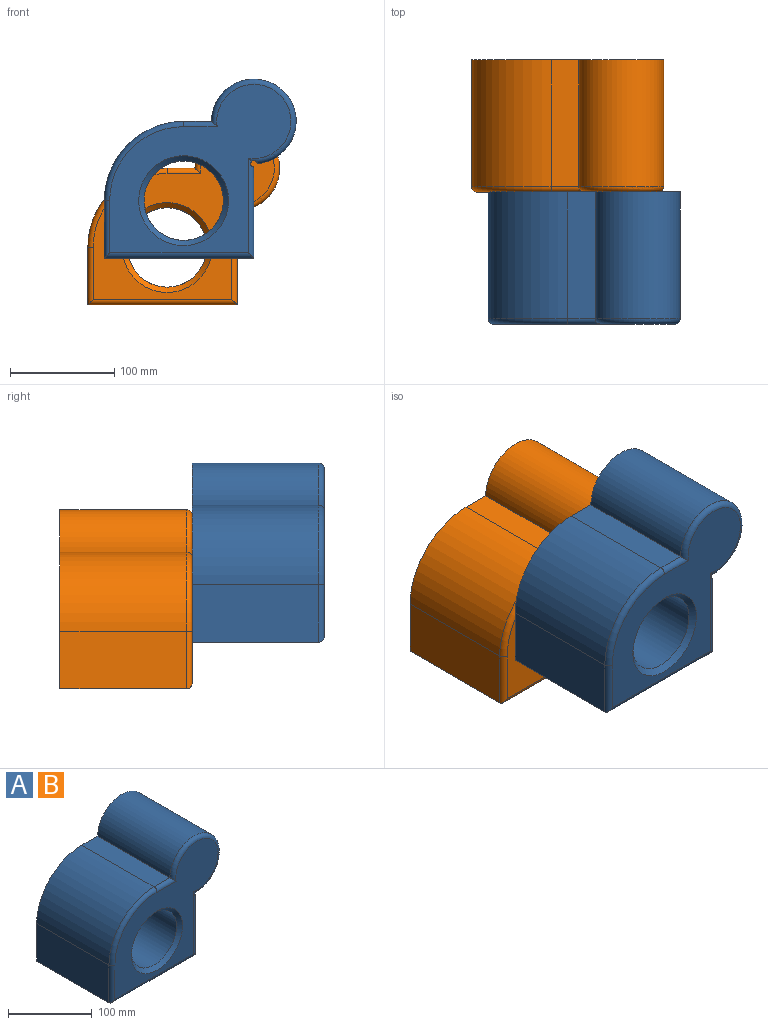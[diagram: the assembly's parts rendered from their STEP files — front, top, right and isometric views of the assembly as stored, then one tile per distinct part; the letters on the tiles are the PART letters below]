
ASSEMBLY  parts=2 mates=1
PART A: 17 faces, bbox 194x127x175.5 mm
  f0: plane 121.92x87.55mm, normal (1,0,0), area 10673.5mm2, adj f3,f7,f9,f14
  f1: cylinder r=40.72mm len=121.92mm, axis (0,1,0), area 23007.2mm2, adj f2,f4,f9,f14
  f2: torus R=35.64mm, axis (0,-1,0), area 1469.4mm2, adj f1,f3,f8,f10,f14
  f3: cylinder r=5.08mm len=96.16mm, axis (0,0,-1), area 702.5mm2, adj f0,f2,f8,f12,f14
  f4: plane 121.92x26.72mm, normal (0,0,1), area 3258mm2, adj f1,f5,f9,f10
  f5: cylinder r=76.2mm len=121.92mm, axis (0,1,0), area 14593.2mm2, adj f4,f6,f9,f11
  f6: plane 121.92x55.24mm, normal (-1,0,0), area 6734.7mm2, adj f5,f7,f9,f13
  f7: plane 143.64x121.92mm, normal (0,0,-1), area 17512.7mm2, adj f0,f6,f9,f12
  f8: plane 174.2x162mm, normal (0,-1,0), area 12573.2mm2, adj f2,f3,f10,f11,f12,f13,f16
  f9: plane 184.36x172.16mm, normal (0,1,0), area 16956.6mm2, adj f0,f1,f4,f5,f6,f7,f14,f15
  f10: cylinder r=5.08mm len=32.17mm, axis (1,0,0), area 228.6mm2, adj f2,f4,f8,f11
  f11: torus R=71.12mm, axis (0,-1,0), area 932mm2, adj f5,f8,f10,f13
  f12: cylinder r=5.08mm len=143.64mm, axis (-1,0,0), area 1116.7mm2, adj f3,f7,f8,f13
  f13: cylinder r=5.08mm len=55.24mm, axis (0,0,1), area 426.1mm2, adj f6,f8,f11,f12
  f14: cylinder r=3.17mm len=126.63mm, axis (0,1,0), area 1869.1mm2, adj f0,f1,f2,f3,f9
  f15: cylinder r=38.1mm len=121.92mm, axis (0,1,0), area 29186.4mm2, adj f9,f16
  f16: cone r=43.18mm half-angle=45deg, axis (0,-1,0), area 1834.5mm2, adj f8,f15
PART B: same geometry as A
PLACE A t=(-288.5,-56.08,13.28)mm
PLACE B t=(-304.42,70.92,-31.69)mm
MATE planar B.f8 <-> A.f9  axis (0,-1,0) through (-287.29,-56.08,64.98)mm
